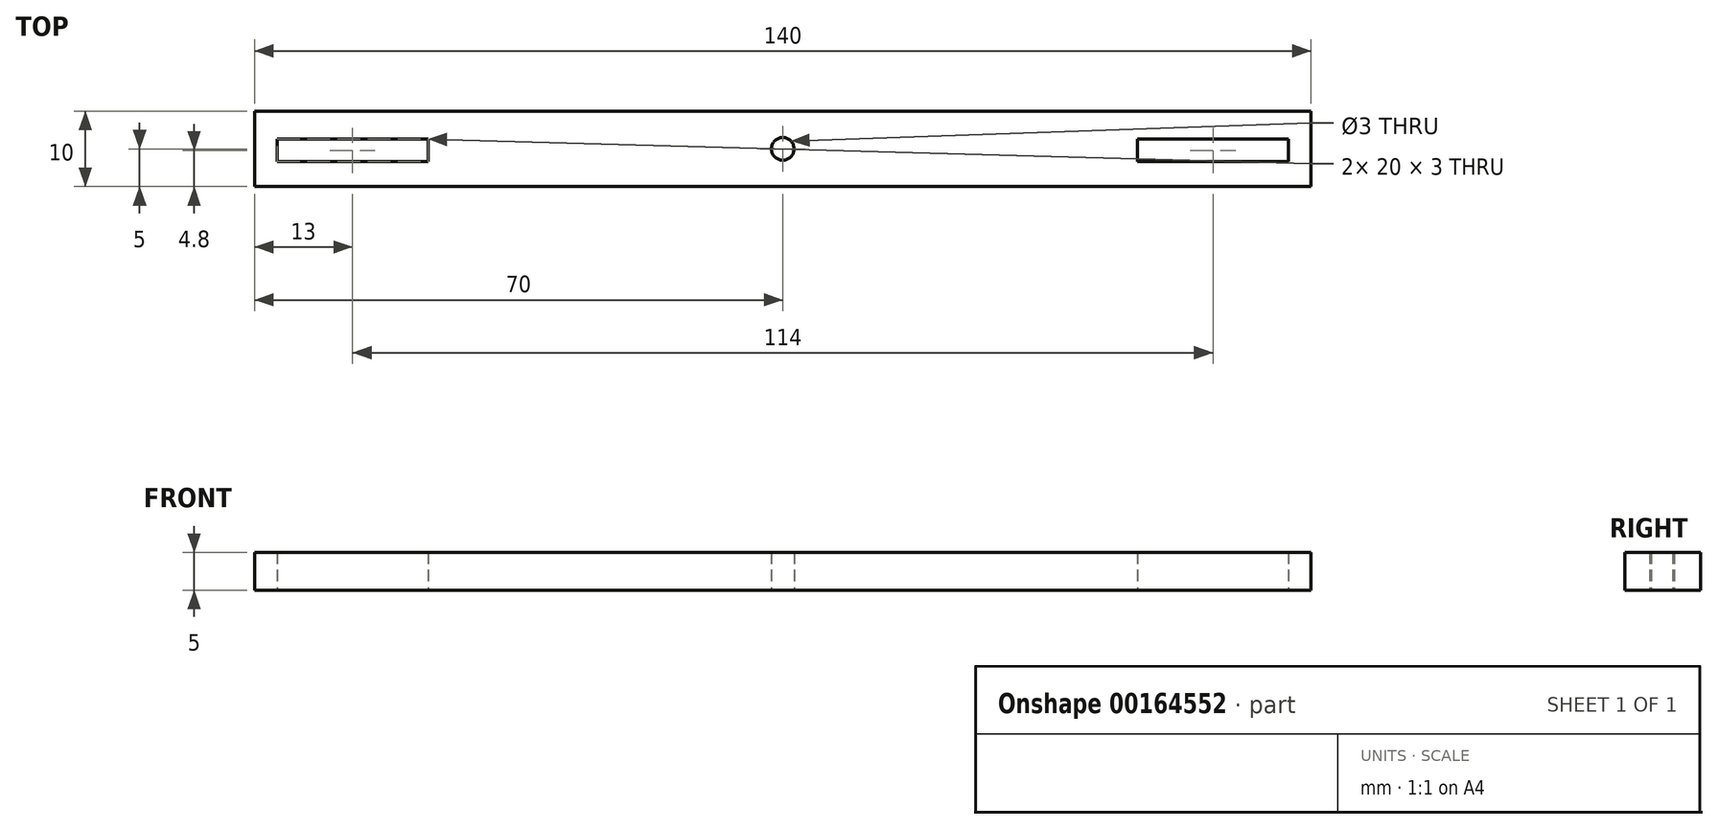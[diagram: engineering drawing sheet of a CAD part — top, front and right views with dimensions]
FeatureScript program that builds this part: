
annotation { "Feature Type Name" : "Feature", "Feature Type Description" : "" }
export const myFeature = defineFeature(function(context is Context, id is Id, definition is map)
    precondition{}
    {
        {
            var Q0;
            Q0=qCreatedBy(makeId("Top.planeOp"),FACE);
            var sketch = newSketch(context, id + "F0", { "sketchPlane" : qUnion([Q0])});
            skLineSegment(sketch, "E0.bottom", {"start": v(0, 0) * mm, "end": v(140, 0) * mm});
            skLineSegment(sketch, "E0.top", {"start": v(0, 10) * mm, "end": v(140, 10) * mm});
            skLineSegment(sketch, "E0.left", {"start": v(0, 0) * mm, "end": v(0, 10) * mm});
            skLineSegment(sketch, "E0.right", {"start": v(140, 0) * mm, "end": v(140, 10) * mm});
            skLineSegment(sketch, "E1.bottom", {"start": v(3, 3.3) * mm, "end": v(23, 3.3) * mm});
            skLineSegment(sketch, "E1.top", {"start": v(3, 6.3) * mm, "end": v(23, 6.3) * mm});
            skLineSegment(sketch, "E1.left", {"start": v(3, 3.3) * mm, "end": v(3, 6.3) * mm});
            skLineSegment(sketch, "E1.right", {"start": v(23, 3.3) * mm, "end": v(23, 6.3) * mm});
            skLineSegment(sketch, "E2.bottom", {"start": v(117, 3.3) * mm, "end": v(137, 3.3) * mm});
            skLineSegment(sketch, "E2.top", {"start": v(117, 6.3) * mm, "end": v(137, 6.3) * mm});
            skLineSegment(sketch, "E2.left", {"start": v(117, 3.3) * mm, "end": v(117, 6.3) * mm});
            skLineSegment(sketch, "E2.right", {"start": v(137, 3.3) * mm, "end": v(137, 6.3) * mm});
            skCircle(sketch, "E3", {"center": v(70, 5) * mm, "radius": 1.5 * mm});
            skSolve(sketch);
        }
        {
            var Q0;
            Q0=makeQuery(id+"F0.imprint","IMPRINT",FACE,{"disambiguationData":[TD([[makeQuery(id+"F0.imprint","IMPRINT",EDGE,{"derivedFrom":sQuery(id+"F0.wireOp",EDGE,"E0.bottom")}),1.0]])]});
            extrude(context, id + "F1", {"entities" : qUnion([Q0]), "depth" : 5 * mm});
        }
    });
